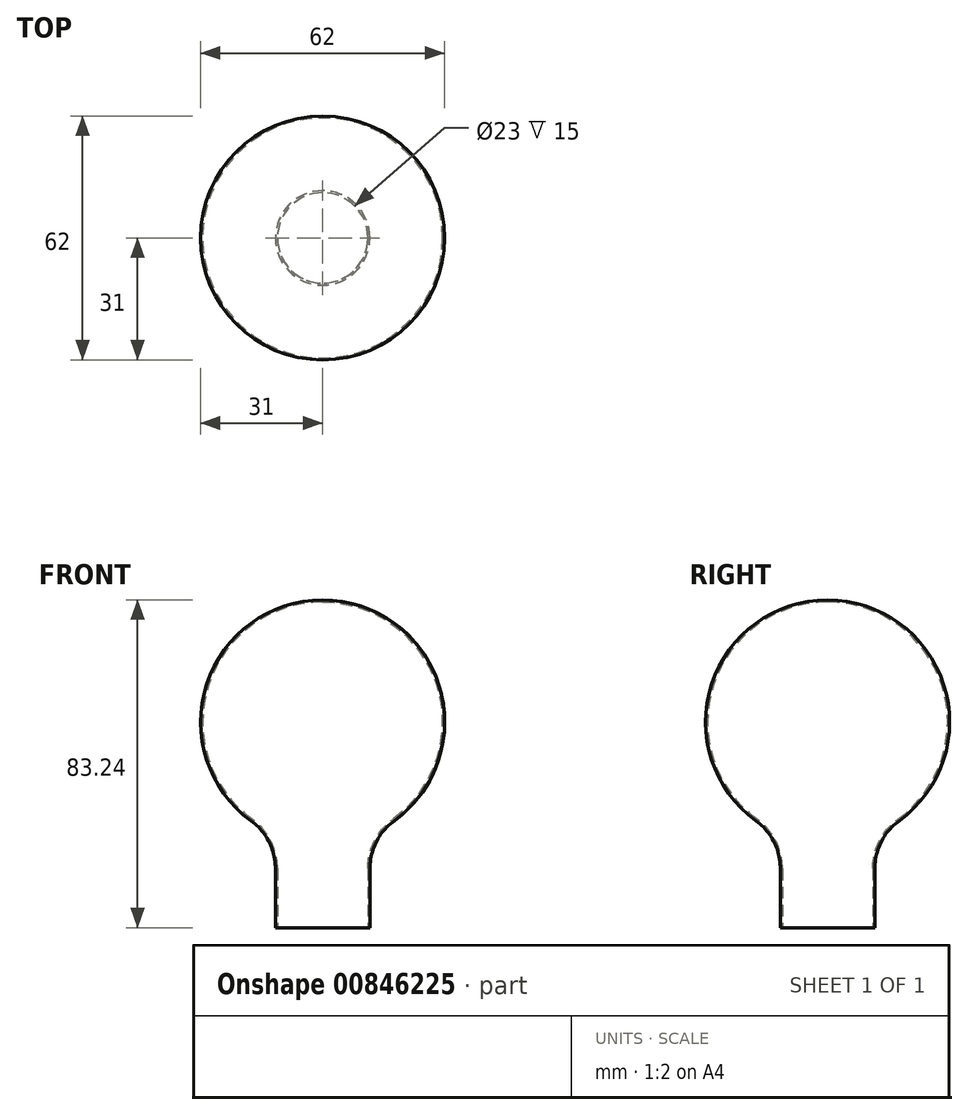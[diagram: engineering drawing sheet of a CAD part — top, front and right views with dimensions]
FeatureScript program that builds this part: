
annotation { "Feature Type Name" : "Feature", "Feature Type Description" : "" }
export const myFeature = defineFeature(function(context is Context, id is Id, definition is map)
    precondition{}
    {
        {
            var Q0;
            Q0=qCreatedBy(makeId("Front.planeOp"),FACE);
            var sketch = newSketch(context, id + "F0", { "sketchPlane" : qUnion([Q0])});
            skArc(sketch, "E0", {"start": v(18.2, 27.14) * mm, "mid": v(29.49, 61.8) * mm, "end": v(0, 83.24) * mm});
            skLineSegment(sketch, "E1", {"start": v(12, 15) * mm, "end": v(12, 0) * mm});
            skLineSegment(sketch, "E2", {"start": v(12, 0) * mm, "end": v(0, 0) * mm});
            skLineSegment(sketch, "E3", {"start": v(0, 0) * mm, "end": v(0, 83.24) * mm});
            skPoint(sketch, "E4.newPointA", {"position": v(0, 21.24) * mm});
            skArc(sketch, "E4.filletArc", {"start": v(18.2, 27.14) * mm, "mid": v(13.64, 21.82) * mm, "end": v(12, 15) * mm});
            skSolve(sketch);
        }
        {
            var Q0;
            Q0=makeQuery(id+"F0.imprint","IMPRINT",FACE,{"disambiguationData":[TD([[makeQuery(id+"F0.imprint","IMPRINT",EDGE,{"derivedFrom":sQuery(id+"F0.wireOp",EDGE,"E0")}),1.0]])]});
            var Q1;
            Q1=sQuery(id+"F0.wireOp",EDGE,"E3");
            revolve(context, id + "F1", {"surfaceOperationType" : NewSurfaceOperationType.NEW, "entities" : qUnion([Q0]), "axis" : qUnion([Q1]), "revolveType" : RevolveType.FULL});
        }
        {
            var Q0;
            Q0=makeQuery(id+"F1.opRevolve","SWEPT_FACE",FACE,{"disambiguationData":[OSD([sQuery(id+"F0.wireOp",EDGE,"E2")])]});
            shell(context, id + "F2", {"entities" : qUnion([Q0]), "thickness" : 0.5 * mm});
        }
    });
